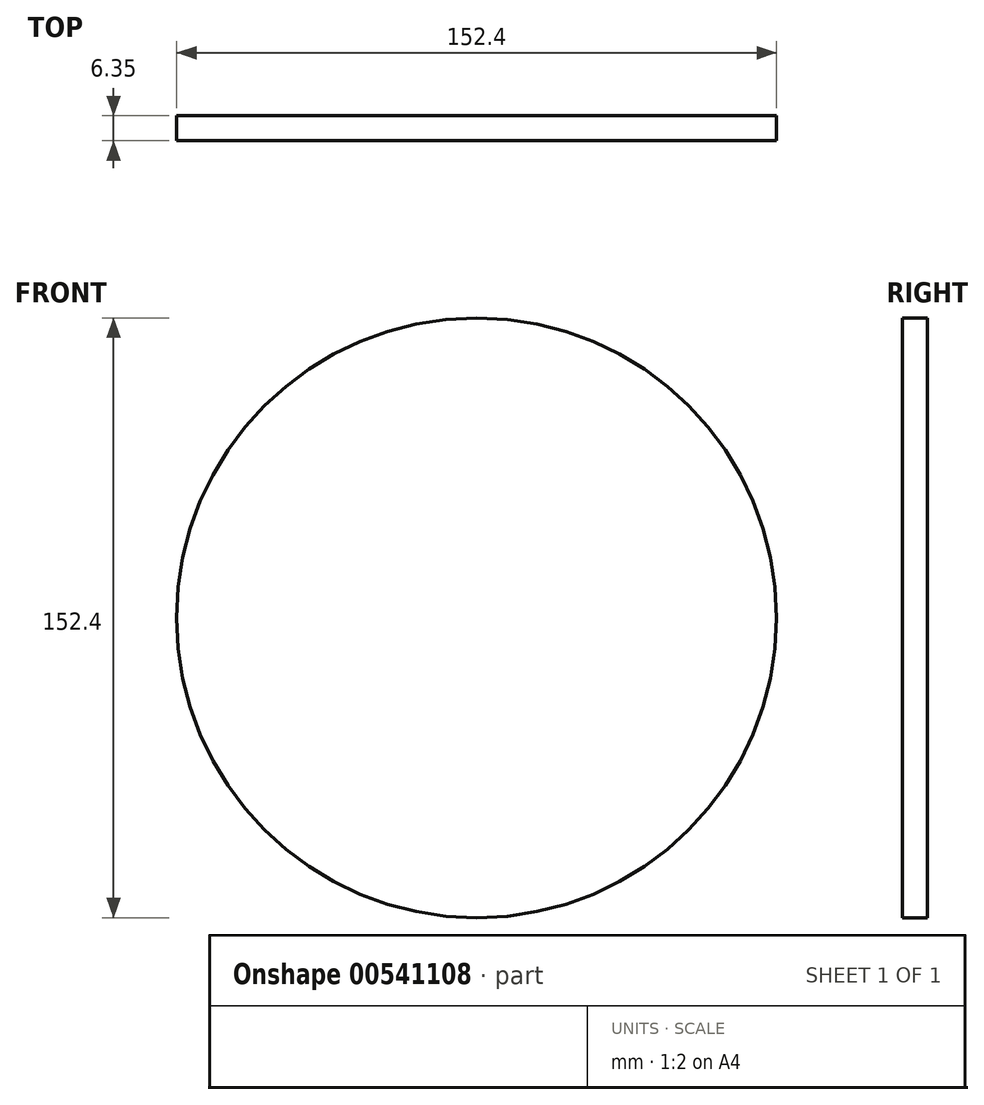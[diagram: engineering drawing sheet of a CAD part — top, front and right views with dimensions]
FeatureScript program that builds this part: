
annotation { "Feature Type Name" : "Feature", "Feature Type Description" : "" }
export const myFeature = defineFeature(function(context is Context, id is Id, definition is map)
    precondition{}
    {
        {
            var Q0;
            Q0=qCreatedBy(makeId("Front.planeOp"),FACE);
            var sketch = newSketch(context, id + "F0", { "sketchPlane" : qUnion([Q0])});
            skCircle(sketch, "E0", {"center": v(0, 0) * mm, "radius": 76.2 * mm});
            skSolve(sketch);
        }
        {
            var Q0;
            Q0 = qSketchRegion(id + "F0", true);
            extrude(context, id + "F1", {"entities" : qUnion([Q0]), "depth" : 6.35 * mm, "offsetDistance" : 25.4 * mm});
        }
    });
